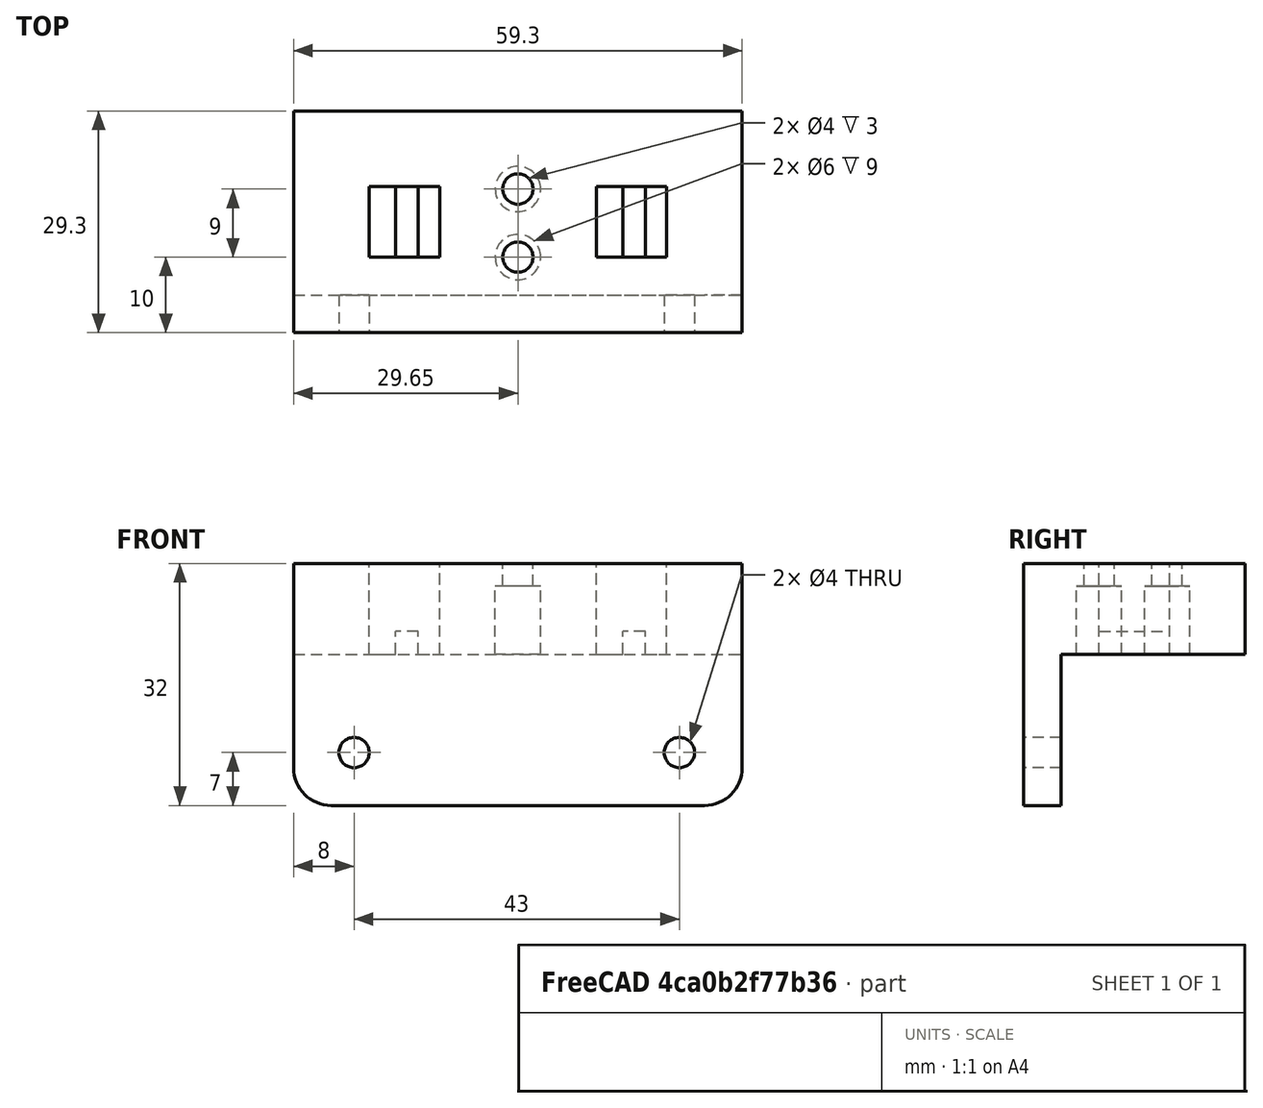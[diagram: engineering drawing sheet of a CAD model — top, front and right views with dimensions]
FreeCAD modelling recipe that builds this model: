
FCSTD DOCUMENT  (FreeCAD 0.16R6703 (Git))
Label: Interruptores Soporte
License: All rights reserved
LicenseURL: http://en.wikipedia.org/wiki/All_rights_reserved
objects: Part::Box×6, Part::Cylinder×6, Part::MultiFuse×4, Part::Cut×3, Part::Fillet×1
note: 20 computed .brp shape members not serialized (recipe doc carries the construction recipe); baked Part::Feature solids carry a one-line shape summary decoded from their .brp

FEATURE [Part::Box] Box  label="Cube"
  Height = 12
  Length = 9.3
  Placement = pos=(30,0,0) rot=(0,0,1;0rad)
  Width = 9.3
FEATURE [Part::Box] Box001  label="Cube001"
  Height = 3
  Length = 3
  Placement = pos=(3.5,0,0) rot=(0,0,1;0rad)
  Width = 10
FEATURE [Part::Box] Box003  label="Cube003"
  Height = 12
  Length = 59.3
  Placement = pos=(-10,-10,0) rot=(0,0,1;0rad)
  Width = 29.3
FEATURE [Part::Box] Box004  label="Cube004"
  Height = 3
  Length = 3
  Placement = pos=(33.5,0,0) rot=(0,0,1;0rad)
  Width = 10
FEATURE [Part::Box] Box005  label="Cube005"
  Height = 12
  Length = 9.3
  Width = 9.3
FEATURE [Part::Cylinder] Cylinder001
  Angle = 360
  Height = 10
  Placement = pos=(19.65,9,-5) rot=(0,0,1;0rad)
  Radius = 3
FEATURE [Part::Box] Box006  label="Cube006"
  Height = 20
  Length = 59.3
  Placement = pos=(-10,-10,-20) rot=(0,0,1;0rad)
  Width = 5
FEATURE [Part::Cylinder] Cylinder002
  Angle = 360
  Height = 10
  Placement = pos=(-2,0,-13) rot=(1,0,0;1.5708rad)
  Radius = 2
FEATURE [Part::Cylinder] Cylinder003
  Angle = 360
  Height = 10
  Placement = pos=(41,0,-13) rot=(1,0,0;1.5708rad)
  Radius = 2
FEATURE [Part::MultiFuse] Fusion002
  Shapes = -> [Cylinder003,Cylinder002]
FEATURE [Part::Cylinder] Cylinder004
  Angle = 360
  Height = 10
  Placement = pos=(19.65,0,-5) rot=(0,0,1;0rad)
  Radius = 3
FEATURE [Part::Cylinder] Cylinder005
  Angle = 360
  Height = 3
  Placement = pos=(19.65,9,5) rot=(0,0,1;0rad)
  Radius = 2
FEATURE [Part::Cylinder] Cylinder006
  Angle = 360
  Height = 3
  Placement = pos=(19.65,0,5) rot=(0,0,1;0rad)
  Radius = 2
FEATURE [Part::Fillet] Fillet
  Base = -> Box006
  Edges = 2 edges r=5: [Edge4,Edge8]
FEATURE [Part::MultiFuse] Fusion
  Shapes = -> [Box005,Box]
FEATURE [Part::Cut] Cut
  Base = -> Box003
  Tool = -> Fusion
FEATURE [Part::MultiFuse] Fusion003
  Placement = pos=(0,0,4) rot=(0,0,1;0rad)
  Shapes = -> [Cylinder004,Cylinder005,Cylinder001,Cylinder006]
FEATURE [Part::Cut] Cut001
  Base = -> Cut
  Tool = -> Fusion003
FEATURE [Part::Cut] Cut002
  Base = -> Fillet
  Tool = -> Fusion002
FEATURE [Part::MultiFuse] Fusion004
  Shapes = -> [Box001,Box004,Cut001,Cut002]
